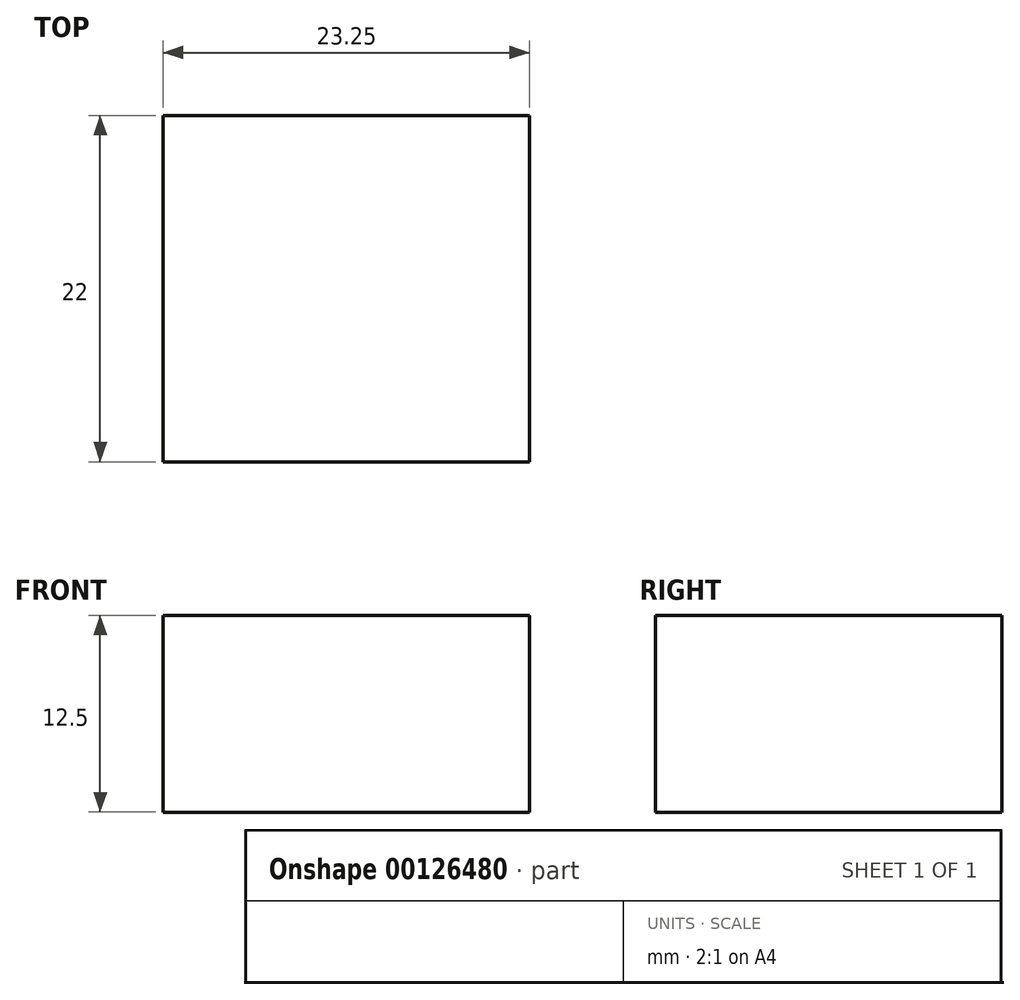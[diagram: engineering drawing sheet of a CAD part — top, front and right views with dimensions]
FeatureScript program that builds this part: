
annotation { "Feature Type Name" : "Feature", "Feature Type Description" : "" }
export const myFeature = defineFeature(function(context is Context, id is Id, definition is map)
    precondition{}
    {
        {
            var Q0;
            Q0=qCreatedBy(makeId("Front.planeOp"),FACE);
            var sketch = newSketch(context, id + "F0", { "sketchPlane" : qUnion([Q0])});
            skLineSegment(sketch, "E0.bottom", {"start": v(-10.34, 8.23) * mm, "end": v(12.9, 8.23) * mm});
            skLineSegment(sketch, "E0.top", {"start": v(-10.34, -4.27) * mm, "end": v(12.9, -4.27) * mm});
            skLineSegment(sketch, "E0.left", {"start": v(-10.34, 8.23) * mm, "end": v(-10.34, -4.27) * mm});
            skLineSegment(sketch, "E0.right", {"start": v(12.9, 8.23) * mm, "end": v(12.9, -4.27) * mm});
            skSolve(sketch);
        }
        {
            var Q0;
            Q0 = qSketchRegion(id + "F0", true);
            extrude(context, id + "F1", {"entities" : qUnion([Q0]), "depth" : 22 * mm});
        }
    });
